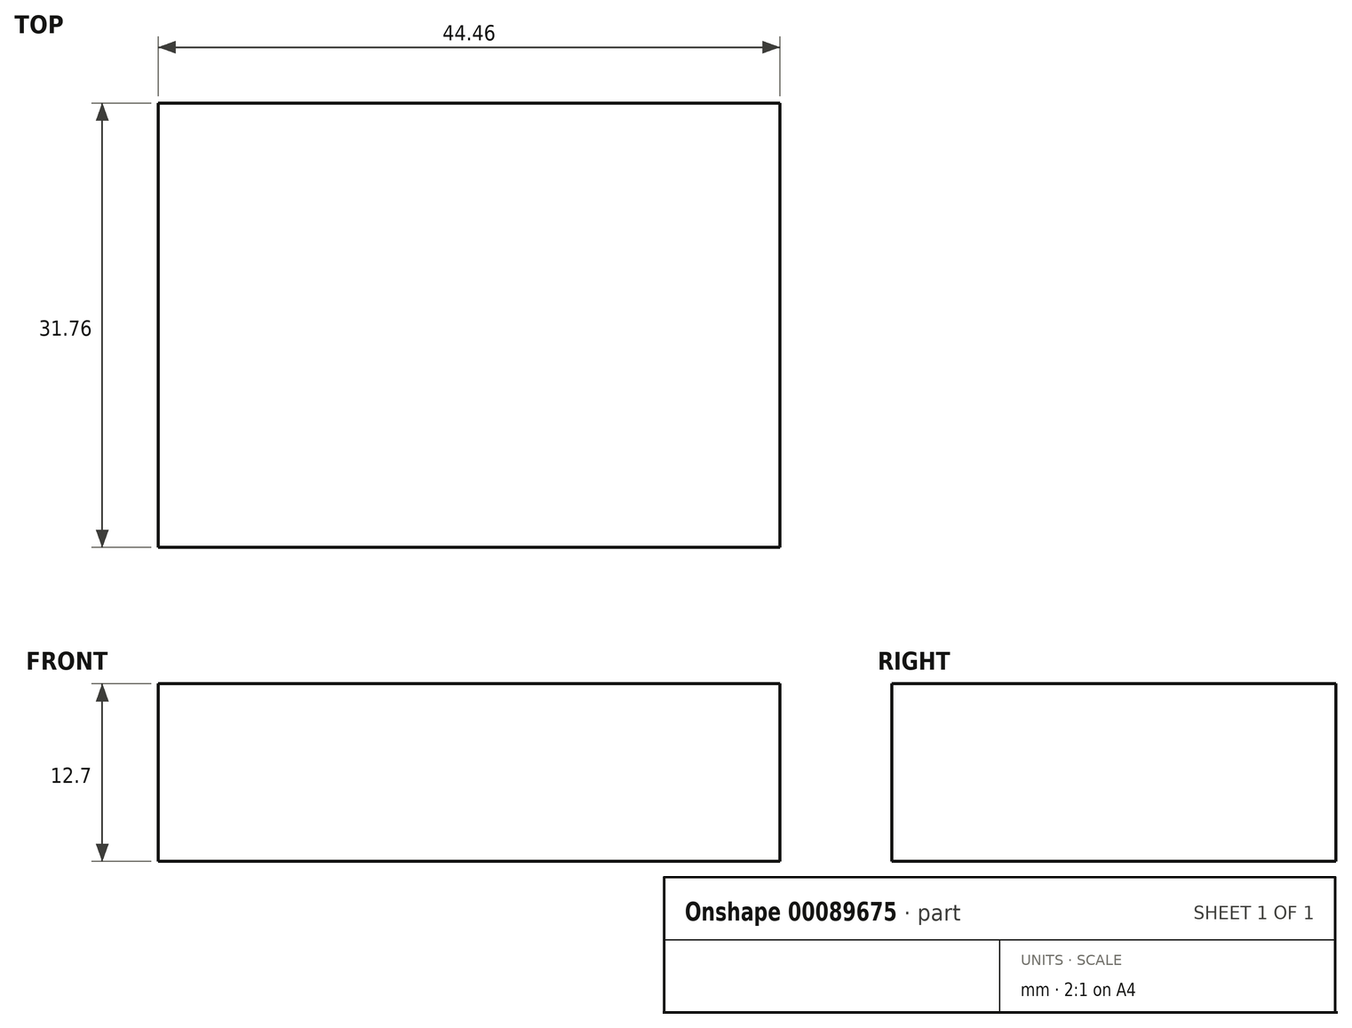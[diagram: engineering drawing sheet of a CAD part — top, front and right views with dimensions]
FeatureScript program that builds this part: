
annotation { "Feature Type Name" : "Feature", "Feature Type Description" : "" }
export const myFeature = defineFeature(function(context is Context, id is Id, definition is map)
    precondition{}
    {
        {
            var Q0;
            Q0=qCreatedBy(makeId("Top.planeOp"),FACE);
            var sketch = newSketch(context, id + "F0", { "sketchPlane" : qUnion([Q0])});
            skLineSegment(sketch, "E0.bottom", {"start": v(22.23, 15.88) * mm, "end": v(-22.22, 15.88) * mm});
            skLineSegment(sketch, "E0.top", {"start": v(22.22, -15.88) * mm, "end": v(-22.23, -15.88) * mm});
            skLineSegment(sketch, "E0.left", {"start": v(22.23, 15.88) * mm, "end": v(22.22, -15.88) * mm});
            skLineSegment(sketch, "E0.right", {"start": v(-22.22, 15.88) * mm, "end": v(-22.23, -15.88) * mm});
            skPoint(sketch, "E0.middle", {"position": v(0, 0) * mm});
            skSolve(sketch);
        }
        {
            var Q0;
            Q0 = qSketchRegion(id + "F0", true);
            extrude(context, id + "F1", {"entities" : qUnion([Q0]), "depth" : 12.7 * mm});
        }
    });
